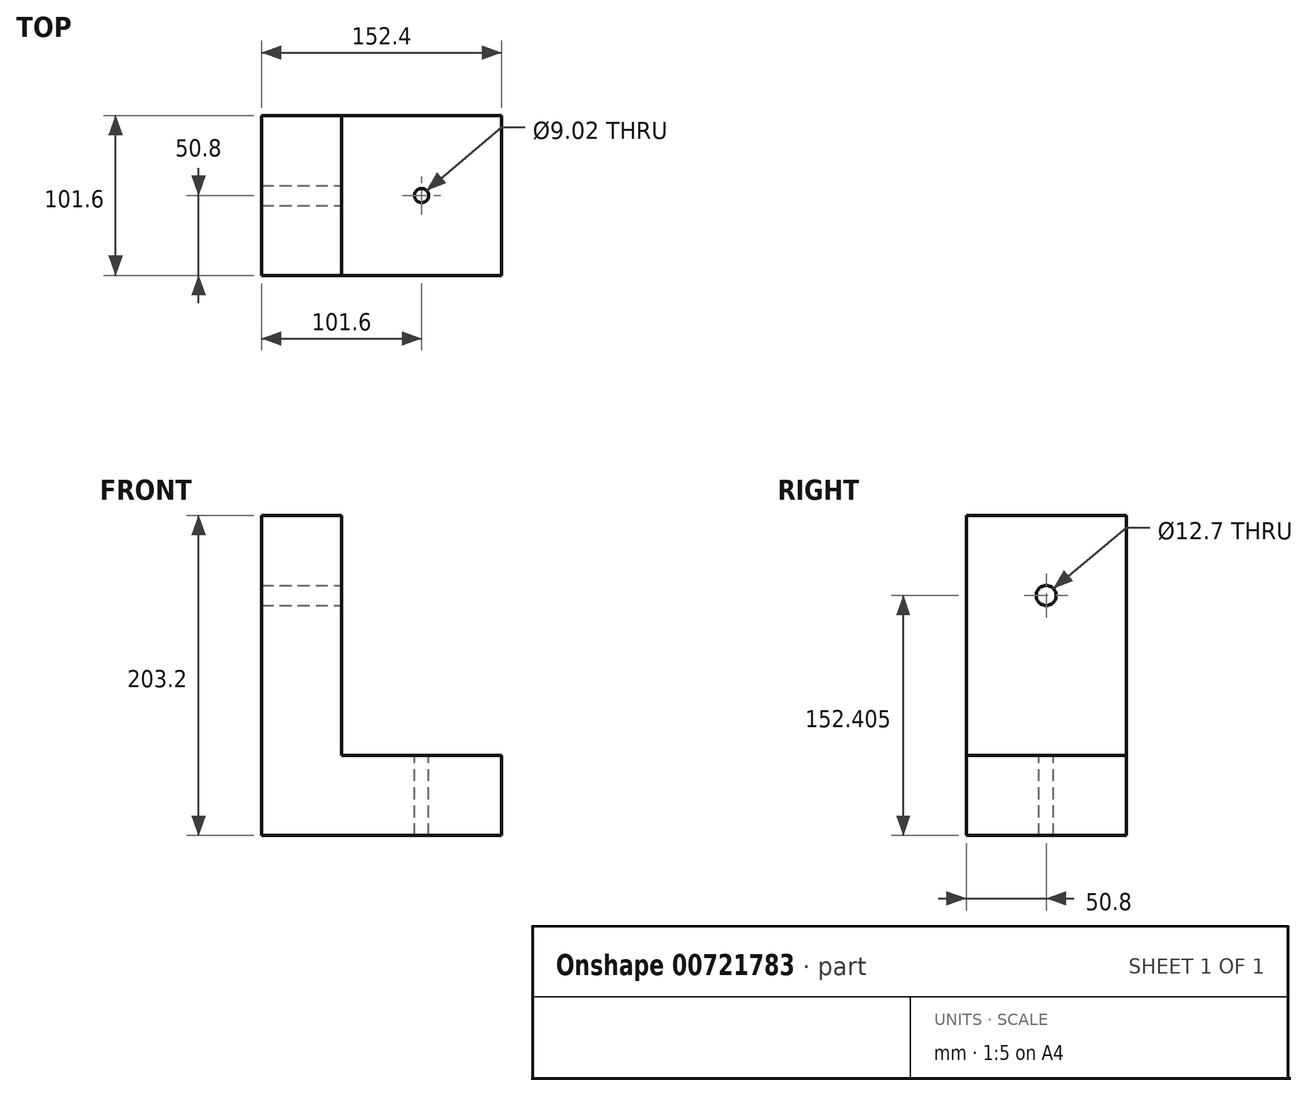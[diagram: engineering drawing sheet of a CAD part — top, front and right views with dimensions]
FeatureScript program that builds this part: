
annotation { "Feature Type Name" : "Feature", "Feature Type Description" : "" }
export const myFeature = defineFeature(function(context is Context, id is Id, definition is map)
    precondition{}
    {
        {
            var Q0;
            Q0=qCreatedBy(makeId("Front.planeOp"),FACE);
            var sketch = newSketch(context, id + "F0", { "sketchPlane" : qUnion([Q0])});
            skLineSegment(sketch, "E0", {"start": v(0, 101.04) * mm, "end": v(0, -102.16) * mm});
            skLineSegment(sketch, "E1", {"start": v(0, -102.16) * mm, "end": v(152.4, -102.16) * mm});
            skLineSegment(sketch, "E2", {"start": v(152.4, -102.16) * mm, "end": v(152.4, -51.36) * mm});
            skLineSegment(sketch, "E3", {"start": v(152.4, -51.36) * mm, "end": v(50.8, -51.36) * mm});
            skLineSegment(sketch, "E4", {"start": v(50.8, -51.36) * mm, "end": v(50.8, 101.04) * mm});
            skLineSegment(sketch, "E5", {"start": v(50.8, 101.04) * mm, "end": v(0, 101.04) * mm});
            skSolve(sketch);
        }
        {
            var Q0;
            Q0=makeQuery(id+"F0.imprint","IMPRINT",FACE,{"disambiguationData":[TD([[makeQuery(id+"F0.imprint","IMPRINT",EDGE,{"derivedFrom":sQuery(id+"F0.wireOp",EDGE,"E0")}),1.0]])]});
            extrude(context, id + "F1", {"entities" : qUnion([Q0]), "depth" : 101.6 * mm, "offsetDistance" : 25.4 * mm});
        }
        {
            var Q0;
            Q0=makeQuery(id+"F1.opExtrude","SWEPT_FACE",FACE,{"disambiguationData":[OSD([sQuery(id+"F0.wireOp",EDGE,"E4")])]});
            var sketch = newSketch(context, id + "F2", { "sketchPlane" : qUnion([Q0])});
            skLineSegment(sketch, "E6", {"start": v(-101.6, 101.04) * mm, "end": v(-50.8, 101.04) * mm});
            skLineSegment(sketch, "E7", {"start": v(-50.8, 101.04) * mm, "end": v(-50.8, 50.24) * mm});
            skCircle(sketch, "E8", {"center": v(-50.8, 50.24) * mm, "radius": 6.35 * mm});
            skSolve(sketch);
        }
        {
            var Q0;
            Q0=makeQuery(id+"F1.opExtrude","SWEPT_FACE",FACE,{"disambiguationData":[OSD([sQuery(id+"F0.wireOp",EDGE,"E3")])]});
            var sketch = newSketch(context, id + "F3", { "sketchPlane" : qUnion([Q0])});
            skLineSegment(sketch, "E9", {"start": v(50.8, -50.8) * mm, "end": v(101.6, -50.8) * mm});
            skPoint(sketch, "E9.endSnap0", {"position": v(50.8, -50.8) * mm});
            skCircle(sketch, "E10", {"center": v(101.6, -50.8) * mm, "radius": 4.5 * mm});
            skSolve(sketch);
        }
        {
            var Q0;
            Q0=makeQuery(id+"F3.imprint","IMPRINT",FACE,{"disambiguationData":[TD([[makeQuery(id+"F3.imprint","IMPRINT",EDGE,{"derivedFrom":sQuery(id+"F3.wireOp",EDGE,"E10")}),1.0]])]});
            extrude(context, id + "F4", {"entities" : qUnion([Q0]), "operationType" : NewBodyOperationType.REMOVE, "oppositeDirection" : true, "depth" : 115.9 * mm, "offsetDistance" : 25.4 * mm});
        }
        {
            var Q0;
            Q0=makeQuery(id+"F2.imprint","IMPRINT",FACE,{"disambiguationData":[TD([[makeQuery(id+"F2.imprint","IMPRINT",EDGE,{"derivedFrom":sQuery(id+"F2.wireOp",EDGE,"E8")}),1.0]])]});
            extrude(context, id + "F5", {"entities" : qUnion([Q0]), "operationType" : NewBodyOperationType.REMOVE, "oppositeDirection" : true, "depth" : 182.8 * mm, "offsetDistance" : 25.4 * mm});
        }
    });
